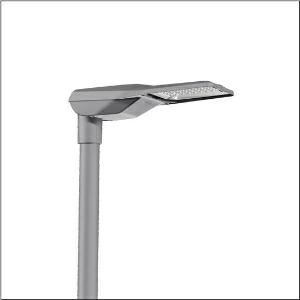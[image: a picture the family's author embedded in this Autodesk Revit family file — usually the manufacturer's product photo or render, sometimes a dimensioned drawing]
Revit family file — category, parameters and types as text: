
# Revit family: streetlight_sl_21_iq_mini___pl52_5xe2h41g08hb_e5d0
name_source: partatom
category: Lighting Fixtures
units: mm (PartAtom-declared; Revit-internal decimal feet)

## family parameters
Cut with Voids When Loaded = No
Host = Face
Light Source = No
Part Type = Normal
Room Calculation Point = No
Round Connector Dimension = Use Diameter
Shared = No

## types (1)
- --- (1 x LED, 9690 lm, 70.9 W, 4000K)
    Apparent Load = 71 VA
    CIE Flux Codes = 27 59 98 100 100
    Color Rendering = 70
    Color Temperature = 4000K
    Default Elevation = 1800 mm
    Description = Streetlight SL 21 iQ mini, mast luminaire, primary light control with lens, of PMMA, primary optical cover: cover, of toughened safety glass, transparent, light distribution: PL52, light emission: direct distribution, primary light characteristic: asymmetric, installation type: post-top, side-entry, LED, High Power LED, rated luminous flux: 9.690lm, luminous efficacy: 137lm/W, light colour: 740, colour temperature: 4000K, control: Street-Remote, Auto-Match, Temp-Guard, Lumen-Switch, Night-Set, Smart-Wire, Light-Fading, Desk-Remote (wireless, voltage-free reading and setting of iQ features in the workshop via application-optimized NFC function/RFID function), optimised constant luminous flux control (CLO 2.0), presetting dimming linear, mains connection: 220..240V, AC, 50/60Hz, start of lifetime: 71W, end of service life: 75W, reduction: 31W, luminaire housing, of diecast aluminium, powder-coated, Siteco® metallic grey (DB 702S), corrosivity category C5 mid according to DIN EN ISO 12944, please order mast flange separately, inclination adjustable: 0°, 5°, 10°, 15°, sealing non-destructively replaceable, multi-level sealing system, length: 628mm, width: 235mm, height: 110mm, mast flange for spigot size: 42mm (side-entry): 5XC10008XM4, 60/48mm (side-entry/post-top): 5XC10108XM2, 76/60mm (side-entry/post-top): 5XC10108XM1, protection rating (complete): IP66, insulation class (complete): insulation class II (safety insulation), certification: CE, ENEC, ENEC+, VDE, impact resistance: IK09, permissible operating ambient temperature for outdoor applications: -40..+50°C, standard-compliant lighting for roads and squares, packaging unit: 1 piece

Light Distribution: PL52
    Height = 110 mm
    Lamp = 1 x LED
    Lamp Light Flux = 9690 lm
    Lamp Power = 70.9 W
    Lamp count = 1
    Length = 625 mm
    Luminous efficacy = 137 lm/W
    Manufacturer = Siteco
    ModVariant = No
    Model = 5XE2H41G08HB
    Number of Poles = 1
    OnlyDefault = Yes
    Power Factor = 1
    Product Name = Streetlight SL 21 iQ mini | PL52
    Product group = mast luminaire | pylon top
    ProductGroupID = 6100
    Protection Class = Protection class II
    Protection Degree = IP 66
    RLX_Detail_Level = 1
    RLX_Emergency_Light_Flux = 0 lm
    RLX_Emergency_Type = 0
    RLX_Emergency_Type_DB = No
    RlxData = <blob elided: 101761 chars, md5=144ef87c>
    Socket = socket
    Standby Power = 0 W
    System Light Flux = 9690 lm
    System Power = 71 W
    Type Comments = factory setting: luminous flux: 100 % | dim-lin: 254 | 711 mA
    Type Image = l_1003519.jpg
    URL = http://relux.com
    VarID = @adj_090685
    Voltage = 0 V
    Weight = 0.00 kg
    Width = 234 mm

## geometry (parser evidence)
native form markers: Blend x4, Sweep x11
no freeform markers — native parametric forms only
